# Revit family: ROCKLED4HTLO-MO-HOWT40120-277V
name_source: partatom
category: Lighting Fixtures
units: mm (PartAtom-declared; Revit-internal decimal feet)

## family parameters
Cut with Voids When Loaded = No
Host = Face
Light Source = Yes
Maintain Annotation Orientation = No
Part Type = Normal
Room Calculation Point = No
Round Connector Dimension = Use Diameter
Shared = No

## types (3) — shared parameters
Color Filter = 16777215
Default Elevation = 1219 mm
Dimming Lamp Color Temperature Shift = <None>
Emit from Line Length = 610 mm
HOUSING MATERIAL = HOUSING MATERIAL
Keynote = Cuerpo: lámina de acero Cal. 22, marco Cal. 14,
acabado con pintura poliéster de aplicación
electrostática. Color blanco RAL9003.
Lamp = LED
Manufacturer = BEGHELLI
Tilt Angle = -90.00°
Type Image = ROCKETLED IMAGE.PNG

## per-type parameters (varying)
| type | Photometric Web File | Wattage Comments |
| ROCKLED4HTLOWT40120-277V | ROCKLED4HTLOWT40120-277V.ies | 109W |
| ROCKLED4HTMOWT40120-277V | ROCKLED4HTMOWT40120-277V.ies | 146W |
| ROCKLED4HTHOWT40120-277V | ROCKLED4HTHOWT40120-277V.ies | 194W |

note: column(s) folded — value = type name in every type: Model

## geometry (parser evidence)
native form markers: Sweep x5
no freeform markers — native parametric forms only
